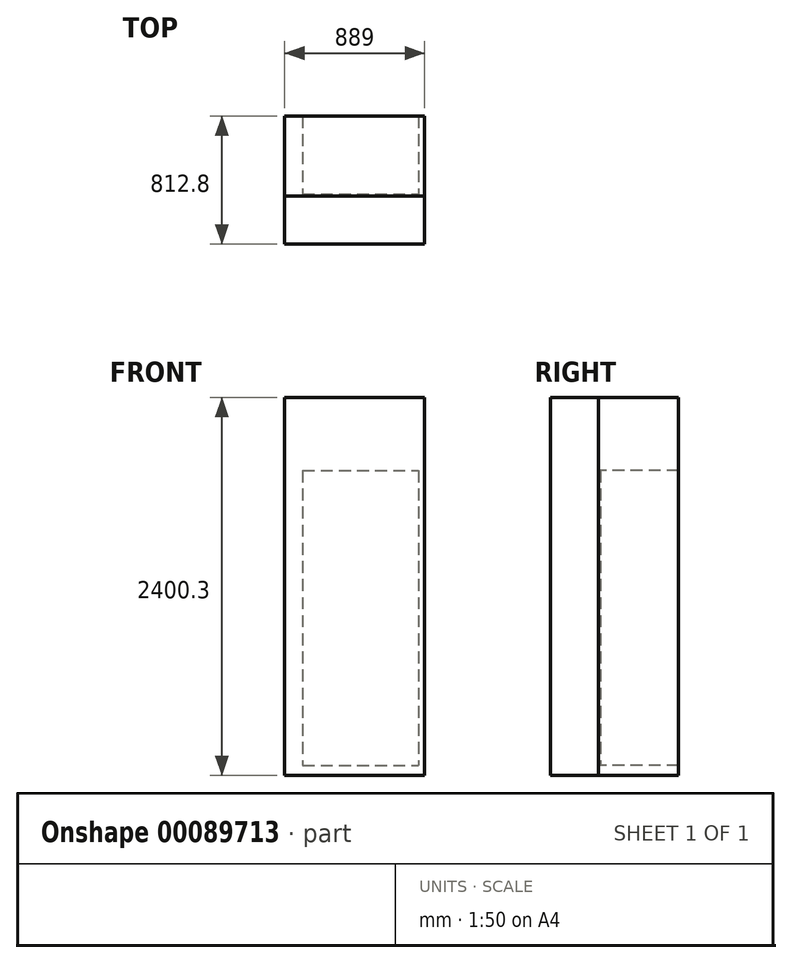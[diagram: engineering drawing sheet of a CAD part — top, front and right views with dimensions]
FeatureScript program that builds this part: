
annotation { "Feature Type Name" : "Feature", "Feature Type Description" : "" }
export const myFeature = defineFeature(function(context is Context, id is Id, definition is map)
    precondition{}
    {
        {
            var Q0;
            Q0=qCreatedBy(makeId("Top.planeOp"),FACE);
            var sketch = newSketch(context, id + "F0", { "sketchPlane" : qUnion([Q0])});
            skLineSegment(sketch, "E0.bottom", {"start": v(444.5, 254) * mm, "end": v(-444.5, 254) * mm});
            skLineSegment(sketch, "E0.top", {"start": v(444.5, -254) * mm, "end": v(-444.5, -254) * mm});
            skLineSegment(sketch, "E0.left", {"start": v(444.5, 254) * mm, "end": v(444.5, -254) * mm});
            skLineSegment(sketch, "E0.right", {"start": v(-444.5, 254) * mm, "end": v(-444.5, -254) * mm});
            skPoint(sketch, "E0.middle", {"position": v(0, 0) * mm});
            skSolve(sketch);
        }
        {
            var Q0;
            Q0 = qSketchRegion(id + "F0", true);
            extrude(context, id + "F1", {"entities" : qUnion([Q0]), "depth" : 2400.3 * mm});
        }
        {
            var Q0;
            Q0=qCreatedBy(makeId("Top.planeOp"),FACE);
            var sketch = newSketch(context, id + "F2", { "sketchPlane" : qUnion([Q0])});
            skLineSegment(sketch, "E1.bottom", {"start": v(-444.5, -254) * mm, "end": v(444.5, -254) * mm});
            skLineSegment(sketch, "E1.top", {"start": v(-444.5, -558.8) * mm, "end": v(444.5, -558.8) * mm});
            skLineSegment(sketch, "E1.left", {"start": v(-444.5, -254) * mm, "end": v(-444.5, -558.8) * mm});
            skLineSegment(sketch, "E1.right", {"start": v(444.5, -254) * mm, "end": v(444.5, -558.8) * mm});
            skSolve(sketch);
        }
        {
            var Q0;
            Q0 = qSketchRegion(id + "F2", true);
            extrude(context, id + "F3", {"entities" : qUnion([Q0]), "depth" : 2400.3 * mm});
        }
        {
            var Q0;
            Q0=makeQuery(id+"F1.opExtrude","CAP_FACE",FACE,{"disambiguationData":[OSD([sQuery(id+"F0.wireOp",EDGE,"E0.bottom"),sQuery(id+"F0.wireOp",EDGE,"E0.top"),sQuery(id+"F0.wireOp",EDGE,"E0.left"),sQuery(id+"F0.wireOp",EDGE,"E0.right")])],"isStart":true});
            cPlane(context, id + "F4", {"entities" : qUnion([Q0]), "cplaneType" : CPlaneType.OFFSET, "offset" : 63.5 * mm, "oppositeDirection" : true, "width" : 152.4 * mm, "height" : 152.4 * mm});
        }
        {
            var Q0;
            Q0=qCreatedBy(id+"F4.planeOp",FACE);
            var sketch = newSketch(context, id + "F5", { "sketchPlane" : qUnion([Q0])});
            skLineSegment(sketch, "E2.bottom", {"start": v(-330.2, -254) * mm, "end": v(406.4, -254) * mm});
            skLineSegment(sketch, "E2.top", {"start": v(-330.2, 241.3) * mm, "end": v(406.4, 241.3) * mm});
            skLineSegment(sketch, "E2.left", {"start": v(-330.2, -254) * mm, "end": v(-330.2, 241.3) * mm});
            skLineSegment(sketch, "E2.right", {"start": v(406.4, -254) * mm, "end": v(406.4, 241.3) * mm});
            skSolve(sketch);
        }
        {
            var Q0;
            Q0 = qSketchRegion(id + "F5", true);
            extrude(context, id + "F6", {"entities" : qUnion([Q0]), "oppositeDirection" : true, "depth" : 1873.25 * mm});
        }
    });
